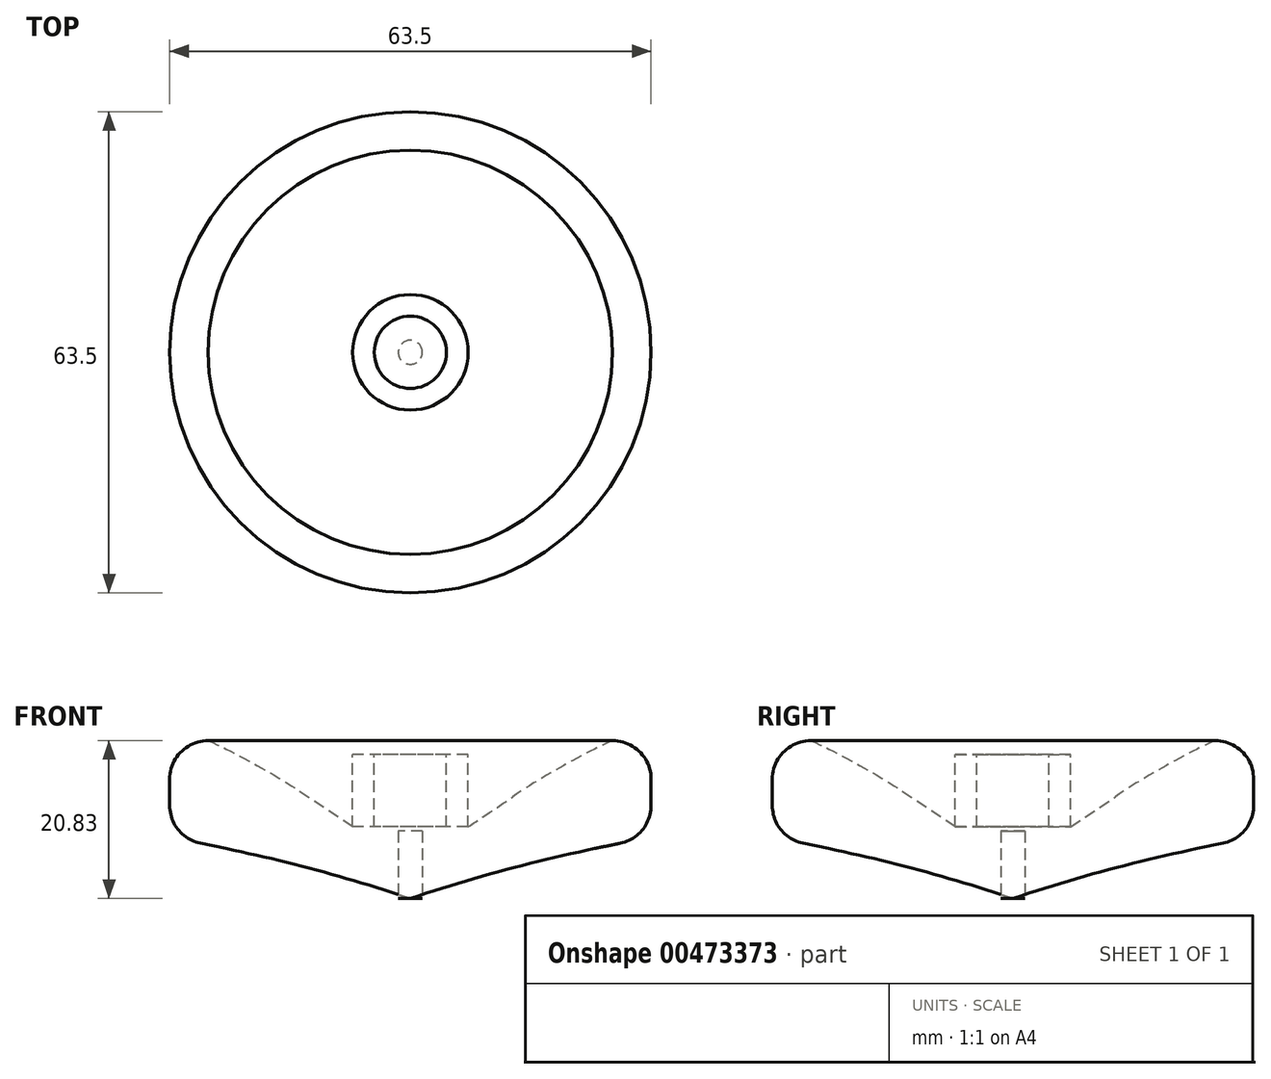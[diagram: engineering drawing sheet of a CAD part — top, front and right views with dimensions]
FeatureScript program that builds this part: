
annotation { "Feature Type Name" : "Feature", "Feature Type Description" : "" }
export const myFeature = defineFeature(function(context is Context, id is Id, definition is map)
    precondition{}
    {
        {
            var Q0;
            Q0=qCreatedBy(makeId("Front.planeOp"),FACE);
            var sketch = newSketch(context, id + "F0", { "sketchPlane" : qUnion([Q0])});
            skLineSegment(sketch, "E0", {"start": v(31.75, 8.13) * mm, "end": v(31.75, 20.83) * mm});
            skLineSegment(sketch, "E1", {"start": v(31.75, 20.83) * mm, "end": v(24.44, 20.83) * mm});
            skLineSegment(sketch, "E2", {"start": v(24.44, 20.83) * mm, "end": v(7.62, 9.44) * mm});
            skLineSegment(sketch, "E3", {"start": v(7.62, 9.44) * mm, "end": v(7.62, 18.96) * mm});
            skLineSegment(sketch, "E4", {"start": v(7.62, 18.96) * mm, "end": v(0, 18.96) * mm});
            skLineSegment(sketch, "E5", {"start": v(0, 18.96) * mm, "end": v(0, 0) * mm});
            skLineSegment(sketch, "E6", {"start": v(0, 0) * mm, "end": v(11.98, 4.02) * mm});
            skLineSegment(sketch, "E7", {"start": v(11.98, 4.02) * mm, "end": v(31.75, 8.13) * mm});
            skSolve(sketch);
        }
        {
            var Q0;
            Q0=qSketchRegion(id+"F0",true);
            var Q1;
            Q1=sQuery(id+"F0.wireOp",EDGE,"E5");
            revolve(context, id + "F1", {"entities" : qUnion([Q0]), "axis" : qUnion([Q1]), "revolveType" : RevolveType.FULL});
        }
        {
            var Q0;
            Q0=makeQuery(id+"F1.opRevolve","SWEPT_FACE",FACE,{"disambiguationData":[OSD([sQuery(id+"F0.wireOp",EDGE,"E0")])]});
            fillet(context, id + "F2", {"entities" : qUnion([Q0]), "radius" : 5.08 * mm, "tangentPropagation" : true, "allowEdgeOverflow" : false});
        }
        {
            var Q0;
            Q0=makeQuery(id+"F1.opRevolve","SWEPT_EDGE",EDGE,{"disambiguationData":[OSD([sQuery(id+"F0.wireOp",EDGE,"E1"),sQuery(id+"F0.wireOp",EDGE,"E2")])]});
            var Q1;
            {var subQ0=sQuery(id+"F0.wireOp",EDGE,"E1");Q1=makeQuery(id+"F2.opFillet","BLEND_EDGE",EDGE,{"blendedFrom":[makeQuery(id+"F1.opRevolve","SWEPT_EDGE",EDGE,{"disambiguationData":[OSD([sQuery(id+"F0.wireOp",EDGE,"E0"),subQ0])]}),makeQuery(id+"F1.opRevolve","SWEPT_FACE",FACE,{"disambiguationData":[OSD([subQ0])]})],"blendedInto":[makeQuery(id+"F1.opRevolve","SWEPT_FACE",FACE,{"disambiguationData":[OSD([subQ0])]})]});}
            fillet(context, id + "F3", {"entities" : qUnion([Q0, Q1]), "radius" : 91.44 * mm, "tangentPropagation" : true, "allowEdgeOverflow" : false});
        }
        {
            var Q0;
            Q0=makeQuery(id+"F1.opRevolve","SWEPT_EDGE",EDGE,{"disambiguationData":[OSD([sQuery(id+"F0.wireOp",EDGE,"E6"),sQuery(id+"F0.wireOp",EDGE,"E7")])]});
            var Q1;
            {var subQ0=sQuery(id+"F0.wireOp",EDGE,"E7");Q1=makeQuery(id+"F2.opFillet","BLEND_EDGE",EDGE,{"blendedFrom":[makeQuery(id+"F1.opRevolve","SWEPT_EDGE",EDGE,{"disambiguationData":[OSD([sQuery(id+"F0.wireOp",EDGE,"E0"),subQ0])]}),makeQuery(id+"F1.opRevolve","SWEPT_FACE",FACE,{"disambiguationData":[OSD([subQ0])]})],"blendedInto":[makeQuery(id+"F1.opRevolve","SWEPT_FACE",FACE,{"disambiguationData":[OSD([subQ0])]})]});}
            fillet(context, id + "F4", {"entities" : qUnion([Q0, Q1]), "radius" : 213.36 * mm, "tangentPropagation" : true, "allowEdgeOverflow" : false});
        }
        {
            var Q0;
            Q0=makeQuery(id+"F1.opRevolve","SWEPT_FACE",FACE,{"disambiguationData":[OSD([sQuery(id+"F0.wireOp",EDGE,"E4")])]});
            var sketch = newSketch(context, id + "F5", { "sketchPlane" : qUnion([Q0])});
            skCircle(sketch, "E8", {"center": v(0, 0) * mm, "radius": 4.76 * mm});
            skSolve(sketch);
        }
        {
            var Q0;
            Q0=qSketchRegion(id+"F5",true);
            extrude(context, id + "F6", {"entities" : qUnion([Q0]), "oppositeDirection" : true, "depth" : 9.52 * mm});
        }
        {
            var Q0;
            Q0=qCreatedBy(makeId("Top.planeOp"),FACE);
            var sketch = newSketch(context, id + "F7", { "sketchPlane" : qUnion([Q0])});
            skCircle(sketch, "E9", {"center": v(0, 0) * mm, "radius": 1.59 * mm});
            skSolve(sketch);
        }
        {
            var Q0;
            Q0 = qSketchRegion(id + "F7", true);
            extrude(context, id + "F8", {"entities" : qUnion([Q0]), "depth" : 8.9 * mm});
        }
    });
